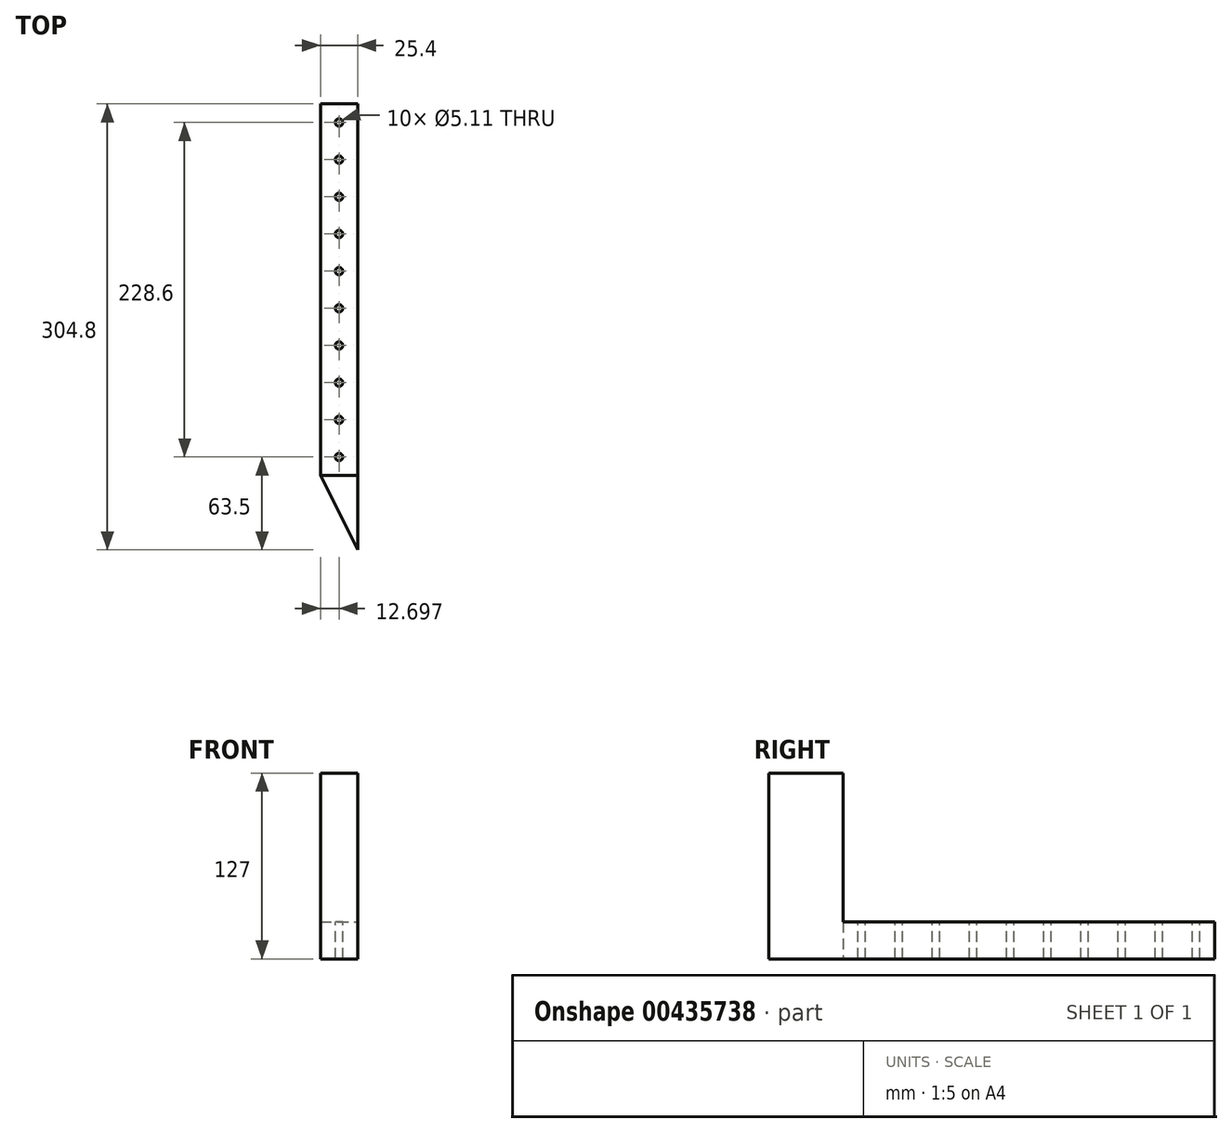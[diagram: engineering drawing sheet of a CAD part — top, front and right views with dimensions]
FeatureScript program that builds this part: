
annotation { "Feature Type Name" : "Feature", "Feature Type Description" : "" }
export const myFeature = defineFeature(function(context is Context, id is Id, definition is map)
    precondition{}
    {
        {
            var Q0;
            Q0=qCreatedBy(makeId("Top.planeOp"),FACE);
            var sketch = newSketch(context, id + "F0", { "sketchPlane" : qUnion([Q0])});
            skLineSegment(sketch, "E0.bottom", {"start": v(-10.58, 177.8) * mm, "end": v(14.82, 177.8) * mm});
            skLineSegment(sketch, "E0.top", {"start": v(-10.58, -76.2) * mm, "end": v(14.82, -76.2) * mm});
            skLineSegment(sketch, "E0.left", {"start": v(-10.58, 177.8) * mm, "end": v(-10.58, -76.2) * mm});
            skLineSegment(sketch, "E0.right", {"start": v(14.82, 177.8) * mm, "end": v(14.82, -76.2) * mm});
            skLineSegment(sketch, "E1", {"start": v(14.82, -76.2) * mm, "end": v(14.82, -127) * mm});
            skLineSegment(sketch, "E2", {"start": v(14.82, -127) * mm, "end": v(-10.58, -76.2) * mm});
            skSolve(sketch);
        }
        {
            var Q0;
            Q0=makeQuery(id+"F0.imprint","IMPRINT",FACE,{"disambiguationData":[TD([[makeQuery(id+"F0.imprint","IMPRINT",EDGE,{"derivedFrom":sQuery(id+"F0.wireOp",EDGE,"E0.top")}),-1.0]])]});
            extrude(context, id + "F1", {"entities" : qUnion([Q0]), "depth" : 127 * mm});
        }
        {
            var Q0;
            Q0=makeQuery(id+"F0.imprint","IMPRINT",FACE,{"disambiguationData":[TD([[makeQuery(id+"F0.imprint","IMPRINT",EDGE,{"derivedFrom":sQuery(id+"F0.wireOp",EDGE,"E0.bottom")}),-1.0]])]});
            extrude(context, id + "F2", {"entities" : qUnion([Q0]), "operationType" : NewBodyOperationType.ADD, "depth" : 25.4 * mm});
        }
        {
            var Q0;
            Q0=makeQuery(id+"F2.opExtrude","CAP_FACE",FACE,{"disambiguationData":[OSD([sQuery(id+"F0.wireOp",EDGE,"E0.bottom"),sQuery(id+"F0.wireOp",EDGE,"E0.top"),sQuery(id+"F0.wireOp",EDGE,"E0.left"),sQuery(id+"F0.wireOp",EDGE,"E0.right")])],"isStart":false});
            var sketch = newSketch(context, id + "F3", { "sketchPlane" : qUnion([Q0])});
            skCircle(sketch, "E3", {"center": v(2.12, 165.1) * mm, "radius": 2.55 * mm});
            skCircle(sketch, "E4.0.1.0", {"center": v(2.12, 139.7) * mm, "radius": 2.55 * mm});
            skCircle(sketch, "E4.0.2.0", {"center": v(2.12, 114.3) * mm, "radius": 2.55 * mm});
            skCircle(sketch, "E4.0.3.0", {"center": v(2.12, 88.9) * mm, "radius": 2.55 * mm});
            skCircle(sketch, "E4.0.4.0", {"center": v(2.12, 63.5) * mm, "radius": 2.55 * mm});
            skCircle(sketch, "E4.0.5.0", {"center": v(2.12, 38.1) * mm, "radius": 2.55 * mm});
            skCircle(sketch, "E4.0.6.0", {"center": v(2.12, 12.7) * mm, "radius": 2.55 * mm});
            skCircle(sketch, "E4.0.7.0", {"center": v(2.12, -12.7) * mm, "radius": 2.55 * mm});
            skCircle(sketch, "E4.0.8.0", {"center": v(2.12, -38.1) * mm, "radius": 2.55 * mm});
            skCircle(sketch, "E4.0.9.0", {"center": v(2.12, -63.5) * mm, "radius": 2.55 * mm});
            skLineSegment(sketch, "E4.direction1", {"start": v(2.12, 165.1) * mm, "end": v(27.52, 165.1) * mm, "construction": true});
            skLineSegment(sketch, "E4.direction2", {"start": v(2.12, 165.1) * mm, "end": v(2.12, 139.7) * mm, "construction": true});
            skSolve(sketch);
        }
        {
            var Q0;
            Q0=sQuery(id+"F3.wireOp",VERTEX,"E4.0.7.0.center");
            var Q1;
            Q1=sQuery(id+"F3.wireOp",VERTEX,"E4.0.6.0.center");
            var Q2;
            Q2=sQuery(id+"F3.wireOp",VERTEX,"E4.0.5.0.center");
            var Q3;
            Q3=sQuery(id+"F3.wireOp",VERTEX,"E4.0.4.0.center");
            var Q4;
            Q4=sQuery(id+"F3.wireOp",VERTEX,"E4.0.3.0.center");
            var Q5;
            Q5=sQuery(id+"F3.wireOp",VERTEX,"E4.0.2.0.center");
            var Q6;
            Q6=sQuery(id+"F3.wireOp",VERTEX,"E4.0.1.0.center");
            var Q7;
            Q7=sQuery(id+"F3.wireOp",VERTEX,"E3.center");
            var Q8;
            Q8=sQuery(id+"F3.wireOp",VERTEX,"E4.0.8.0.center");
            var Q9;
            Q9=sQuery(id+"F3.wireOp",VERTEX,"E4.0.9.0.center");
            var Q10;
            Q10=makeQuery(id+"F1.opExtrude","SWEPT_BODY",BODY,{"disambiguationData":[OSD([sQuery(id+"F0.wireOp",EDGE,"E0.top"),sQuery(id+"F0.wireOp",EDGE,"E1"),sQuery(id+"F0.wireOp",EDGE,"E2")])]});
            hole(context, id + "F4", {"style" : HoleStyle.SIMPLE, "endStyle" : HoleEndStyle.THROUGH, "holeDiameter" : 5.1 * mm, "isTappedThrough" : true, "tappedDepth" : 12.7 * mm, "tapClearance" : 3, "locations" : qUnion([Q0, Q1, Q2, Q3, Q4, Q5, Q6, Q7, Q8, Q9]), "scope" : qUnion([Q10])});
        }
    });
